# Revit family: KEUCO_59552019522
name_source: partatom
category: Allgemeines Modell
revit_build: Autodesk Revit 2016 (Build: 20150220_1215(x64)
units: mm (PartAtom-declared; Revit-internal decimal feet)

## family parameters
Arbeitsebenenbasiert = Ja
Beim Laden mit Abzugskörper schneiden = Nein
Bemaßung runder Anschluss = Durchmesser verwenden
Gemeinsam genutzt = Nein
Immer vertikal = Nein
Kann Basisbauteil für Bewehrung sein = Nein
Raumberechnungspunkt = Nein
Teiletyp = Normal

## types (1)
- 59552019522
    Artikelnummer = 59552019522
    Ausschreibungstext = KEUCO Set IXMO - SOLO  59552019522
Einhebelmischer mit integriertem Schlauchanschluss UP DN15
Hochglanzverchromter Einhebelmischer mit Schlauchanschluss für die Dusche 
aus entzinkungsarmen Messing, mit eckiger Rosette, frei positionierbar,
Integrierter Einbautiefenausgleich von 65-95mm, Gehäuse schallentkoppelt,
Hochwertige Mischwasserkartusche mit keramischen Dichtscheiben und Temperaturbegrenzung,
Fertigset bestehend aus:
Hebel, Hülse, Rosette (eckig) und Funktionseinheit,
Gesamthöhe mit Griff 130 mm, Rosette 90 x 90 mm,
Stärke 10 mm, Gesamtausladung 89 mm

Inklusive KEUCO IXMO - SOLO UP Funktionseinheit  
UP Funktionseinheit für Einhebelmischer mit integriertem Schlauchanschluss, DN15, 
Schallentkoppelter Grundkörper für den Wandeinbau, frei positionierbar,  
Einbautiefe 65 mm – 95 mm, 
Grundplatte für 4 Befestigungsschrauben (bauseits), 
Anschlüsse G 1/2 Zoll mit farblicher Kennzeichnung
    Beschreibung = bestehend aus:
Einhebelmischer mit Schlauchanschluss, Rosette eckig
(59552 019502) und UP Funktionseinheit (59552 000170)
geräuschgeprüft nach DIN 4109, Geräuschklasse 1,
Durchflussklasse A
    Breite = 45 mm  [stored 0.147638 ft]
    Gewicht = 0
    Hersteller = KEUCO
    Material = Stahl, verchromt
    Serie = Plan
    URL = https://www.keuco.com
    Verwendung = DU / WA
    Vorgabe-Ansicht = 1219 mm

note: [stored X ft] marks values corroborated as IEEE doubles in the binary element streams (Revit-internal decimal feet)

## geometry (parser evidence)
native form markers: Sweep x3
no freeform markers — native parametric forms only
